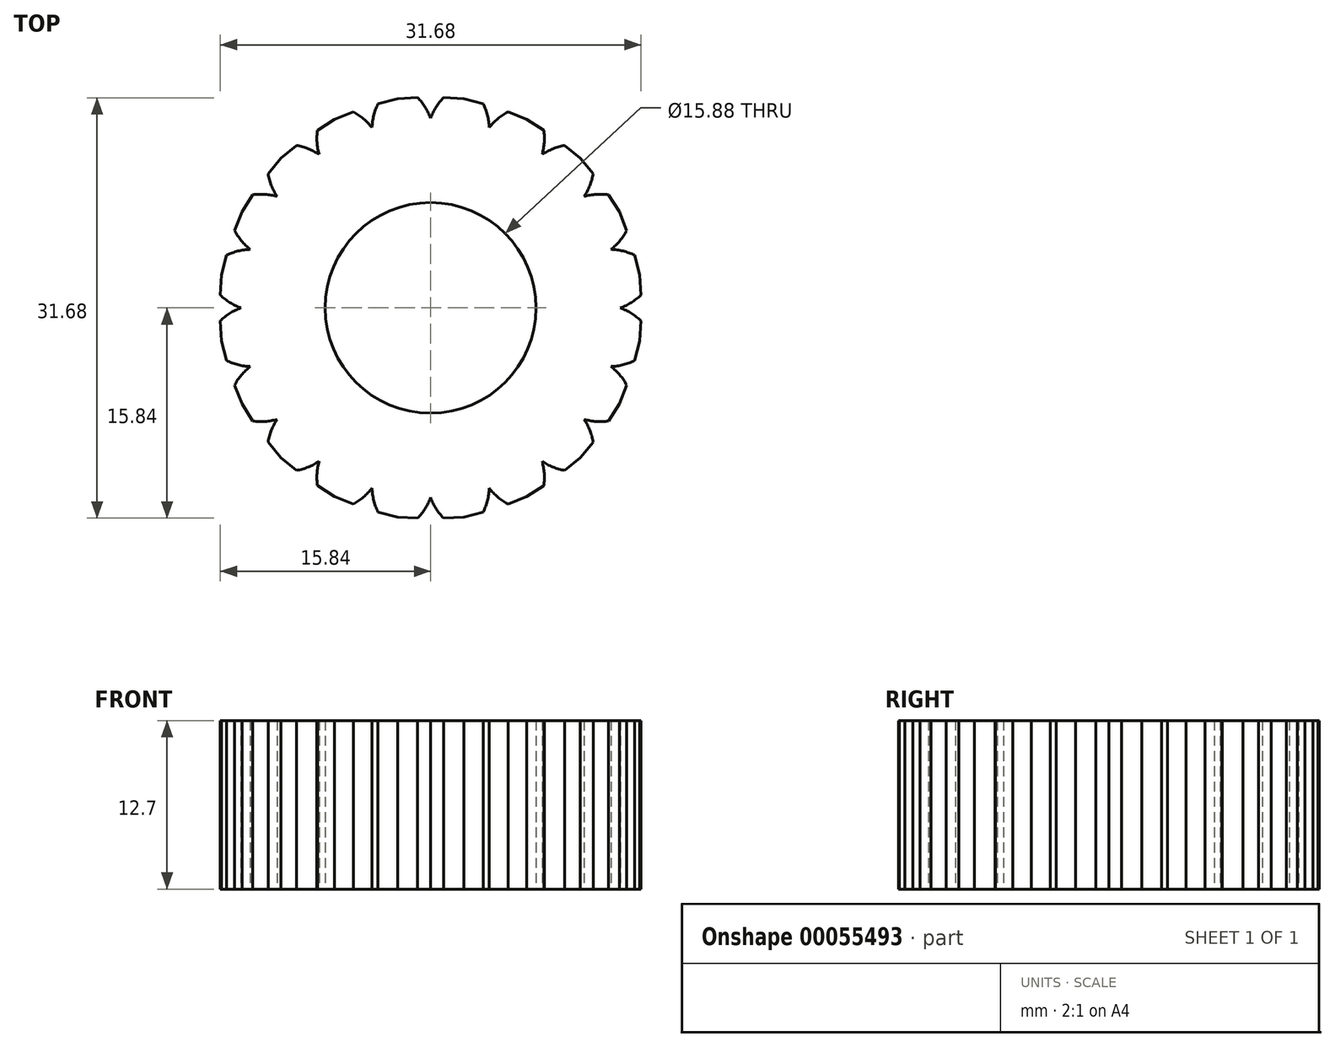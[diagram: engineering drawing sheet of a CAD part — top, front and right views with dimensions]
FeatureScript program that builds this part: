
annotation { "Feature Type Name" : "Feature", "Feature Type Description" : "" }
export const myFeature = defineFeature(function(context is Context, id is Id, definition is map)
    precondition{}
    {
        {
            var Q0;
            Q0=qCreatedBy(makeId("Top.planeOp"),FACE);
            var sketch = newSketch(context, id + "F0", { "sketchPlane" : qUnion([Q0])});
            skCircle(sketch, "E0", {"center": v(0, 0) * mm, "radius": 7.94 * mm});
            skArc(sketch, "E1.trimOffspring", {"start": v(0, 14.29) * mm, "mid": v(-0.4, 15.12) * mm, "end": v(-0.98, 15.84) * mm});
            skLineSegment(sketch, "E2", {"start": v(-0.98, 15.84) * mm, "end": v(-2.5, 15.75) * mm});
            skLineSegment(sketch, "E3", {"start": v(0, 14.29) * mm, "end": v(0, 13.43) * mm});
            skLineSegment(sketch, "E4.MirrorCS", {"start": v(-3.97, 15.37) * mm, "end": v(-2.5, 15.75) * mm});
            skArc(sketch, "E5.MirrorCS", {"start": v(-4.42, 13.59) * mm, "mid": v(-4.28, 14.5) * mm, "end": v(-3.97, 15.37) * mm});
            skLineSegment(sketch, "E6.MirrorCS", {"start": v(-4.42, 13.59) * mm, "end": v(-4.15, 12.77) * mm});
            skLineSegment(sketch, "E7.1.0", {"start": v(-8.52, 13.4) * mm, "end": v(-7.24, 14.2) * mm});
            skArc(sketch, "E7.1.1", {"start": v(-8.4, 11.56) * mm, "mid": v(-8.56, 12.47) * mm, "end": v(-8.52, 13.4) * mm});
            skLineSegment(sketch, "E7.1.2", {"start": v(-8.4, 11.56) * mm, "end": v(-7.9, 10.86) * mm});
            skLineSegment(sketch, "E7.1.3", {"start": v(-5.83, 14.77) * mm, "end": v(-7.24, 14.2) * mm});
            skArc(sketch, "E7.1.4", {"start": v(-4.42, 13.59) * mm, "mid": v(-5.06, 14.25) * mm, "end": v(-5.83, 14.77) * mm});
            skLineSegment(sketch, "E7.2.0", {"start": v(-12.24, 10.1) * mm, "end": v(-11.28, 11.28) * mm});
            skArc(sketch, "E7.2.1", {"start": v(-11.56, 8.4) * mm, "mid": v(-12, 9.22) * mm, "end": v(-12.24, 10.1) * mm});
            skLineSegment(sketch, "E7.2.2", {"start": v(-11.56, 8.4) * mm, "end": v(-10.86, 7.9) * mm});
            skLineSegment(sketch, "E7.2.3", {"start": v(-10.1, 12.24) * mm, "end": v(-11.28, 11.28) * mm});
            skArc(sketch, "E7.2.4", {"start": v(-8.4, 11.56) * mm, "mid": v(-9.22, 12) * mm, "end": v(-10.1, 12.24) * mm});
            skLineSegment(sketch, "E7.2.5", {"start": v(-8.4, 11.56) * mm, "end": v(-7.9, 10.86) * mm});
            skLineSegment(sketch, "E7.3.0", {"start": v(-14.77, 5.83) * mm, "end": v(-14.2, 7.24) * mm});
            skArc(sketch, "E7.3.1", {"start": v(-13.59, 4.42) * mm, "mid": v(-14.25, 5.06) * mm, "end": v(-14.77, 5.83) * mm});
            skLineSegment(sketch, "E7.3.2", {"start": v(-13.59, 4.42) * mm, "end": v(-12.77, 4.15) * mm});
            skLineSegment(sketch, "E7.3.3", {"start": v(-13.4, 8.52) * mm, "end": v(-14.2, 7.24) * mm});
            skArc(sketch, "E7.3.4", {"start": v(-11.56, 8.4) * mm, "mid": v(-12.47, 8.56) * mm, "end": v(-13.4, 8.52) * mm});
            skLineSegment(sketch, "E7.3.5", {"start": v(-11.56, 8.4) * mm, "end": v(-10.86, 7.9) * mm});
            skLineSegment(sketch, "E7.4.0", {"start": v(-15.84, 0.98) * mm, "end": v(-15.75, 2.5) * mm});
            skArc(sketch, "E7.4.1", {"start": v(-14.29, 0) * mm, "mid": v(-15.12, 0.4) * mm, "end": v(-15.84, 0.98) * mm});
            skLineSegment(sketch, "E7.4.2", {"start": v(-14.29, 0) * mm, "end": v(-13.43, 0) * mm});
            skLineSegment(sketch, "E7.4.3", {"start": v(-15.37, 3.97) * mm, "end": v(-15.75, 2.5) * mm});
            skArc(sketch, "E7.4.4", {"start": v(-13.59, 4.42) * mm, "mid": v(-14.5, 4.28) * mm, "end": v(-15.37, 3.97) * mm});
            skLineSegment(sketch, "E7.4.5", {"start": v(-13.59, 4.42) * mm, "end": v(-12.77, 4.15) * mm});
            skLineSegment(sketch, "E7.5.0", {"start": v(-15.37, -3.97) * mm, "end": v(-15.75, -2.5) * mm});
            skArc(sketch, "E7.5.1", {"start": v(-13.59, -4.42) * mm, "mid": v(-14.5, -4.28) * mm, "end": v(-15.37, -3.97) * mm});
            skLineSegment(sketch, "E7.5.2", {"start": v(-13.59, -4.42) * mm, "end": v(-12.77, -4.15) * mm});
            skLineSegment(sketch, "E7.5.3", {"start": v(-15.84, -0.98) * mm, "end": v(-15.75, -2.5) * mm});
            skArc(sketch, "E7.5.4", {"start": v(-14.29, 0) * mm, "mid": v(-15.12, -0.4) * mm, "end": v(-15.84, -0.98) * mm});
            skLineSegment(sketch, "E7.5.5", {"start": v(-14.29, 0) * mm, "end": v(-13.43, 0) * mm});
            skLineSegment(sketch, "E7.6.0", {"start": v(-13.4, -8.52) * mm, "end": v(-14.2, -7.24) * mm});
            skArc(sketch, "E7.6.1", {"start": v(-11.56, -8.4) * mm, "mid": v(-12.47, -8.56) * mm, "end": v(-13.4, -8.52) * mm});
            skLineSegment(sketch, "E7.6.2", {"start": v(-11.56, -8.4) * mm, "end": v(-10.86, -7.9) * mm});
            skLineSegment(sketch, "E7.6.3", {"start": v(-14.77, -5.83) * mm, "end": v(-14.2, -7.24) * mm});
            skArc(sketch, "E7.6.4", {"start": v(-13.59, -4.42) * mm, "mid": v(-14.25, -5.06) * mm, "end": v(-14.77, -5.83) * mm});
            skLineSegment(sketch, "E7.6.5", {"start": v(-13.59, -4.42) * mm, "end": v(-12.77, -4.15) * mm});
            skLineSegment(sketch, "E7.7.0", {"start": v(-10.1, -12.24) * mm, "end": v(-11.28, -11.28) * mm});
            skArc(sketch, "E7.7.1", {"start": v(-8.4, -11.56) * mm, "mid": v(-9.22, -12) * mm, "end": v(-10.1, -12.24) * mm});
            skLineSegment(sketch, "E7.7.2", {"start": v(-8.4, -11.56) * mm, "end": v(-7.9, -10.86) * mm});
            skLineSegment(sketch, "E7.7.3", {"start": v(-12.24, -10.1) * mm, "end": v(-11.28, -11.28) * mm});
            skArc(sketch, "E7.7.4", {"start": v(-11.56, -8.4) * mm, "mid": v(-12, -9.22) * mm, "end": v(-12.24, -10.1) * mm});
            skLineSegment(sketch, "E7.7.5", {"start": v(-11.56, -8.4) * mm, "end": v(-10.86, -7.9) * mm});
            skLineSegment(sketch, "E7.8.0", {"start": v(-5.83, -14.77) * mm, "end": v(-7.24, -14.2) * mm});
            skArc(sketch, "E7.8.1", {"start": v(-4.42, -13.59) * mm, "mid": v(-5.06, -14.25) * mm, "end": v(-5.83, -14.77) * mm});
            skLineSegment(sketch, "E7.8.2", {"start": v(-4.42, -13.59) * mm, "end": v(-4.15, -12.77) * mm});
            skLineSegment(sketch, "E7.8.3", {"start": v(-8.52, -13.4) * mm, "end": v(-7.24, -14.2) * mm});
            skArc(sketch, "E7.8.4", {"start": v(-8.4, -11.56) * mm, "mid": v(-8.56, -12.47) * mm, "end": v(-8.52, -13.4) * mm});
            skLineSegment(sketch, "E7.8.5", {"start": v(-8.4, -11.56) * mm, "end": v(-7.9, -10.86) * mm});
            skLineSegment(sketch, "E7.9.0", {"start": v(-0.98, -15.84) * mm, "end": v(-2.5, -15.75) * mm});
            skArc(sketch, "E7.9.1", {"start": v(0, -14.29) * mm, "mid": v(-0.4, -15.12) * mm, "end": v(-0.98, -15.84) * mm});
            skLineSegment(sketch, "E7.9.2", {"start": v(0, -14.29) * mm, "end": v(0, -13.43) * mm});
            skLineSegment(sketch, "E7.9.3", {"start": v(-3.97, -15.37) * mm, "end": v(-2.5, -15.75) * mm});
            skArc(sketch, "E7.9.4", {"start": v(-4.42, -13.59) * mm, "mid": v(-4.28, -14.5) * mm, "end": v(-3.97, -15.37) * mm});
            skLineSegment(sketch, "E7.9.5", {"start": v(-4.42, -13.59) * mm, "end": v(-4.15, -12.77) * mm});
            skLineSegment(sketch, "E7.10.0", {"start": v(3.97, -15.37) * mm, "end": v(2.5, -15.75) * mm});
            skArc(sketch, "E7.10.1", {"start": v(4.42, -13.59) * mm, "mid": v(4.28, -14.5) * mm, "end": v(3.97, -15.37) * mm});
            skLineSegment(sketch, "E7.10.2", {"start": v(4.42, -13.59) * mm, "end": v(4.15, -12.77) * mm});
            skLineSegment(sketch, "E7.10.3", {"start": v(0.98, -15.84) * mm, "end": v(2.5, -15.75) * mm});
            skArc(sketch, "E7.10.4", {"start": v(0, -14.29) * mm, "mid": v(0.4, -15.12) * mm, "end": v(0.98, -15.84) * mm});
            skLineSegment(sketch, "E7.10.5", {"start": v(0, -14.29) * mm, "end": v(0, -13.43) * mm});
            skLineSegment(sketch, "E7.11.0", {"start": v(8.52, -13.4) * mm, "end": v(7.24, -14.2) * mm});
            skArc(sketch, "E7.11.1", {"start": v(8.4, -11.56) * mm, "mid": v(8.56, -12.47) * mm, "end": v(8.52, -13.4) * mm});
            skLineSegment(sketch, "E7.11.2", {"start": v(8.4, -11.56) * mm, "end": v(7.9, -10.86) * mm});
            skLineSegment(sketch, "E7.11.3", {"start": v(5.83, -14.77) * mm, "end": v(7.24, -14.2) * mm});
            skArc(sketch, "E7.11.4", {"start": v(4.42, -13.59) * mm, "mid": v(5.06, -14.25) * mm, "end": v(5.83, -14.77) * mm});
            skLineSegment(sketch, "E7.11.5", {"start": v(4.42, -13.59) * mm, "end": v(4.15, -12.77) * mm});
            skLineSegment(sketch, "E7.12.0", {"start": v(12.24, -10.1) * mm, "end": v(11.28, -11.28) * mm});
            skArc(sketch, "E7.12.1", {"start": v(11.56, -8.4) * mm, "mid": v(12, -9.22) * mm, "end": v(12.24, -10.1) * mm});
            skLineSegment(sketch, "E7.12.2", {"start": v(11.56, -8.4) * mm, "end": v(10.86, -7.9) * mm});
            skLineSegment(sketch, "E7.12.3", {"start": v(10.1, -12.24) * mm, "end": v(11.28, -11.28) * mm});
            skArc(sketch, "E7.12.4", {"start": v(8.4, -11.56) * mm, "mid": v(9.22, -12) * mm, "end": v(10.1, -12.24) * mm});
            skLineSegment(sketch, "E7.12.5", {"start": v(8.4, -11.56) * mm, "end": v(7.9, -10.86) * mm});
            skLineSegment(sketch, "E7.13.0", {"start": v(14.77, -5.83) * mm, "end": v(14.2, -7.24) * mm});
            skArc(sketch, "E7.13.1", {"start": v(13.59, -4.42) * mm, "mid": v(14.25, -5.06) * mm, "end": v(14.77, -5.83) * mm});
            skLineSegment(sketch, "E7.13.2", {"start": v(13.59, -4.42) * mm, "end": v(12.77, -4.15) * mm});
            skLineSegment(sketch, "E7.13.3", {"start": v(13.4, -8.52) * mm, "end": v(14.2, -7.24) * mm});
            skArc(sketch, "E7.13.4", {"start": v(11.56, -8.4) * mm, "mid": v(12.47, -8.56) * mm, "end": v(13.4, -8.52) * mm});
            skLineSegment(sketch, "E7.13.5", {"start": v(11.56, -8.4) * mm, "end": v(10.86, -7.9) * mm});
            skLineSegment(sketch, "E7.14.0", {"start": v(15.84, -0.98) * mm, "end": v(15.75, -2.5) * mm});
            skArc(sketch, "E7.14.1", {"start": v(14.29, 0) * mm, "mid": v(15.12, -0.4) * mm, "end": v(15.84, -0.98) * mm});
            skLineSegment(sketch, "E7.14.2", {"start": v(14.29, 0) * mm, "end": v(13.43, 0) * mm});
            skLineSegment(sketch, "E7.14.3", {"start": v(15.37, -3.97) * mm, "end": v(15.75, -2.5) * mm});
            skArc(sketch, "E7.14.4", {"start": v(13.59, -4.42) * mm, "mid": v(14.5, -4.28) * mm, "end": v(15.37, -3.97) * mm});
            skLineSegment(sketch, "E7.14.5", {"start": v(13.59, -4.42) * mm, "end": v(12.77, -4.15) * mm});
            skLineSegment(sketch, "E7.15.0", {"start": v(15.37, 3.97) * mm, "end": v(15.75, 2.5) * mm});
            skArc(sketch, "E7.15.1", {"start": v(13.59, 4.42) * mm, "mid": v(14.5, 4.28) * mm, "end": v(15.37, 3.97) * mm});
            skLineSegment(sketch, "E7.15.2", {"start": v(13.59, 4.42) * mm, "end": v(12.77, 4.15) * mm});
            skLineSegment(sketch, "E7.15.3", {"start": v(15.84, 0.98) * mm, "end": v(15.75, 2.5) * mm});
            skArc(sketch, "E7.15.4", {"start": v(14.29, 0) * mm, "mid": v(15.12, 0.4) * mm, "end": v(15.84, 0.98) * mm});
            skLineSegment(sketch, "E7.15.5", {"start": v(14.29, 0) * mm, "end": v(13.43, 0) * mm});
            skLineSegment(sketch, "E7.16.0", {"start": v(13.4, 8.52) * mm, "end": v(14.2, 7.24) * mm});
            skArc(sketch, "E7.16.1", {"start": v(11.56, 8.4) * mm, "mid": v(12.47, 8.56) * mm, "end": v(13.4, 8.52) * mm});
            skLineSegment(sketch, "E7.16.2", {"start": v(11.56, 8.4) * mm, "end": v(10.86, 7.9) * mm});
            skLineSegment(sketch, "E7.16.3", {"start": v(14.77, 5.83) * mm, "end": v(14.2, 7.24) * mm});
            skArc(sketch, "E7.16.4", {"start": v(13.59, 4.42) * mm, "mid": v(14.25, 5.06) * mm, "end": v(14.77, 5.83) * mm});
            skLineSegment(sketch, "E7.16.5", {"start": v(13.59, 4.42) * mm, "end": v(12.77, 4.15) * mm});
            skLineSegment(sketch, "E7.17.0", {"start": v(10.1, 12.24) * mm, "end": v(11.28, 11.28) * mm});
            skArc(sketch, "E7.17.1", {"start": v(8.4, 11.56) * mm, "mid": v(9.22, 12) * mm, "end": v(10.1, 12.24) * mm});
            skLineSegment(sketch, "E7.17.2", {"start": v(8.4, 11.56) * mm, "end": v(7.9, 10.86) * mm});
            skLineSegment(sketch, "E7.17.3", {"start": v(12.24, 10.1) * mm, "end": v(11.28, 11.28) * mm});
            skArc(sketch, "E7.17.4", {"start": v(11.56, 8.4) * mm, "mid": v(12, 9.22) * mm, "end": v(12.24, 10.1) * mm});
            skLineSegment(sketch, "E7.17.5", {"start": v(11.56, 8.4) * mm, "end": v(10.86, 7.9) * mm});
            skLineSegment(sketch, "E7.18.0", {"start": v(5.83, 14.77) * mm, "end": v(7.24, 14.2) * mm});
            skArc(sketch, "E7.18.1", {"start": v(4.42, 13.59) * mm, "mid": v(5.06, 14.25) * mm, "end": v(5.83, 14.77) * mm});
            skLineSegment(sketch, "E7.18.2", {"start": v(4.42, 13.59) * mm, "end": v(4.15, 12.77) * mm});
            skLineSegment(sketch, "E7.18.3", {"start": v(8.52, 13.4) * mm, "end": v(7.24, 14.2) * mm});
            skArc(sketch, "E7.18.4", {"start": v(8.4, 11.56) * mm, "mid": v(8.56, 12.47) * mm, "end": v(8.52, 13.4) * mm});
            skLineSegment(sketch, "E7.18.5", {"start": v(8.4, 11.56) * mm, "end": v(7.9, 10.86) * mm});
            skLineSegment(sketch, "E7.19.0", {"start": v(0.98, 15.84) * mm, "end": v(2.5, 15.75) * mm});
            skArc(sketch, "E7.19.1", {"start": v(0, 14.29) * mm, "mid": v(0.4, 15.12) * mm, "end": v(0.98, 15.84) * mm});
            skLineSegment(sketch, "E7.19.3", {"start": v(3.97, 15.37) * mm, "end": v(2.5, 15.75) * mm});
            skArc(sketch, "E7.19.4", {"start": v(4.42, 13.59) * mm, "mid": v(4.28, 14.5) * mm, "end": v(3.97, 15.37) * mm});
            skLineSegment(sketch, "E7.19.5", {"start": v(4.42, 13.59) * mm, "end": v(4.15, 12.77) * mm});
            skSolve(sketch);
        }
        {
            var Q0;
            Q0=makeQuery(id+"F0.imprint","IMPRINT",FACE,{"disambiguationData":[TD([[makeQuery(id+"F0.imprint","IMPRINT",EDGE,{"derivedFrom":sQuery(id+"F0.wireOp",EDGE,"E0")}),-1.0]])]});
            extrude(context, id + "F1", {"entities" : qUnion([Q0]), "depth" : 12.7 * mm});
        }
    });
